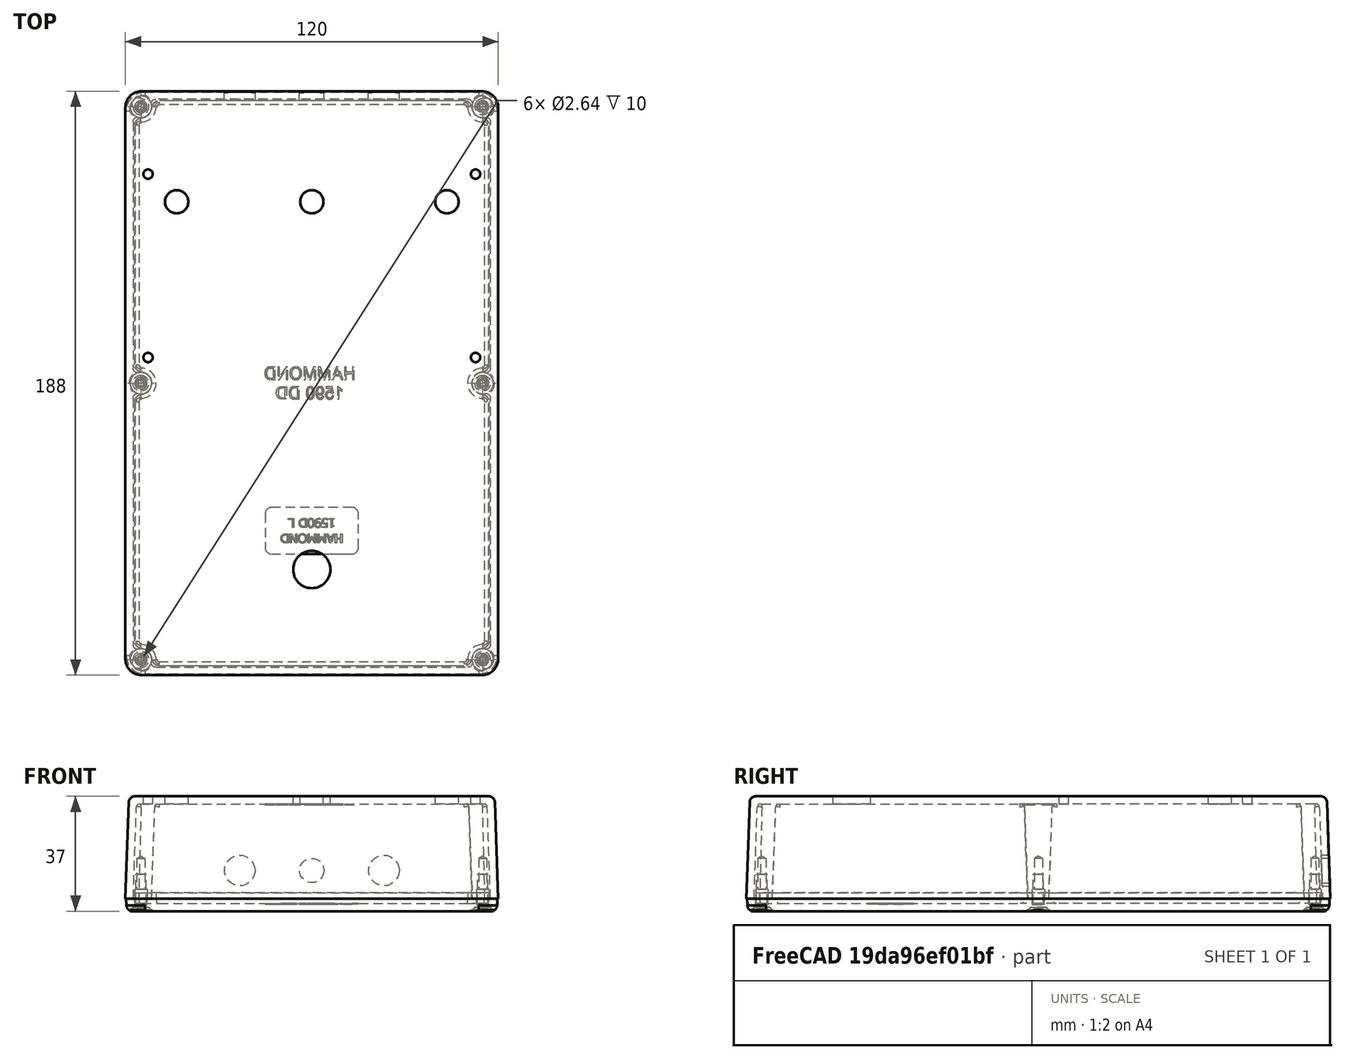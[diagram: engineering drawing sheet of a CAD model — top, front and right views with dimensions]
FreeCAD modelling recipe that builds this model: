
FCSTD DOCUMENT  (FreeCAD 0.19R18750 (Git))
Label: #000-000 - Mu-Tron Phasor II - STEP VRML Spreadsheet
License: All rights reserved
LicenseURL: http://en.wikipedia.org/wiki/All_rights_reserved
objects: Part::Cylinder×11, PartDesign::ShapeBinder×9, Part::Feature×8, App::Part×6, PartDesign::Plane×5, Part::MultiFuse×2, App::VRMLObject×2, PartDesign::Body×1, Part::Cut×1, Spreadsheet::Sheet×1
note: 37 computed .brp shape members not serialized (recipe doc carries the construction recipe); baked Part::Feature solids carry a one-line shape summary decoded from their .brp

FEATURE [PartDesign::Plane] DatumPlane  label="Origin_XY_DatumPlane"
  AttachmentOffset = pos=(-75,-100,0) rot=(0,0,1;0rad)
  Length = 122.361
  MapMode = 5
  Placement = pos=(-75,-100,0) rot=(0,0,1;0rad)
  ResizeMode = 1
  Support = -> [XY_Plane001]
  Width = 200
FEATURE [Part::Feature] Part__Feature  label="#700-001 - 1590DD Box"
  Placement = pos=(0,0,0) rot=(0.707107,0.707107,0;3.14159rad)
  shape: bbox 120 x 188 x 451.1 mm, 273 faces (baked)
FEATURE [Part::Feature] Part__Feature001  label="#700-001 - 1590DD - Lid"
  Placement = pos=(0,0,0) rot=(0,0.707107,0.707107;3.14159rad)
  shape: bbox 187.5 x 5.937 x 119.5 mm, 345 faces (baked)
FEATURE [Part::Feature] Part__Feature002  label="#700-001 - 1590DD - Screw 4/6"
  Placement = pos=(1.2e-14,1.5362,-55) rot=(0,1,0;0.650238rad)
  shape: bbox 6.871 x 11.85 x 6.871 mm, 25 faces (baked)
FEATURE [Part::Feature] Part__Feature003  label="#700-001 - 1590DD - Screw 2/6"
  Placement = pos=(-1.2e-14,1.5362,55) rot=(0,1,0;0.650238rad)
  shape: bbox 6.871 x 11.85 x 6.871 mm, 25 faces (baked)
FEATURE [Part::Feature] Part__Feature004  label="#700-001 - 1590DD - Screw 1/6"
  Placement = pos=(-89,1.5362,55) rot=(0,1,0;0.650238rad)
  shape: bbox 6.871 x 11.85 x 6.871 mm, 25 faces (baked)
FEATURE [Part::Feature] Part__Feature005  label="#700-001 - 1590DD - Screw 3/6"
  Placement = pos=(-89,1.5362,-55) rot=(0,-1,0;0.529817rad)
  shape: bbox 6.871 x 11.85 x 6.871 mm, 25 faces (baked)
FEATURE [Part::Feature] Part__Feature006  label="#700-001 - 1590DD - Screw 5/6"
  Placement = pos=(89,1.5362,55) rot=(0,0,1;0rad)
  shape: bbox 6.871 x 11.85 x 6.871 mm, 25 faces (baked)
FEATURE [Part::Feature] Part__Feature007  label="#700-001 - 1590DD - Screw 6/6"
  Placement = pos=(89,1.5362,-55) rot=(0,0,1;0rad)
  shape: bbox 6.871 x 11.85 x 6.871 mm, 25 faces (baked)
FEATURE [Part::MultiFuse] Fusion  label="#700-000 - Enclosure - Lid & Screws, Fusion"
  Placement = pos=(0,0,0) rot=(0.57735,-0.57735,0.57735;4.18879rad)
  Shapes = -> [Part__Feature001,Part__Feature004,Part__Feature003,Part__Feature005,Part__Feature002,Part__Feature006,Part__Feature007]
FEATURE [Part::Cylinder] Cylinder  label="Drill - Potentiometer - Rate [D=7.5, X=-43.5, Y=58.42]"
  Angle = 360
  AttacherType = Attacher::AttachEngine3D
  Height = 10
  Placement = pos=(-43.498,58.42,25) rot=(0,0,1;0rad)
  Radius = 3.75
FEATURE [Part::Cylinder] Cylinder001  label="Drill - Potentiometer - Depth [D7.5, X=0.0, Y = 58.42]]"
  Angle = 360
  AttacherType = Attacher::AttachEngine3D
  Height = 10
  Placement = pos=(0,58.42,25) rot=(0,0,1;0rad)
  Radius = 3.75
FEATURE [Part::Cylinder] Cylinder002  label="Drill - Potentiometer - Feedback [D=7.5, X=43.5, Y=58.42]"
  Angle = 360
  AttacherType = Attacher::AttachEngine3D
  Height = 10
  Placement = pos=(43.498,58.42,25) rot=(0,0,1;0rad)
  Radius = 3.75
FEATURE [PartDesign::Plane] DatumPlane001  label="Enclosure_Face_XY_DatumPlane"
  Length = 60
  MapMode = 5
  Placement = pos=(0,0,30.5) rot=(1,0,0;3.14159rad)
  ResizeMode = 0
  Width = 60
FEATURE [Part::Cylinder] Cylinder003  label="Drill - Standoff 4/4 [D=3.0, X=-52.705, Y=8.26]"
  Angle = 360
  AttacherType = Attacher::AttachEngine3D
  Height = 10
  Placement = pos=(-52.705,8.26,26) rot=(0,0,1;0rad)
  Radius = 1.5
FEATURE [Part::Cylinder] Cylinder004  label="Drill - Standoff 3/4 [D=3.0, X=52.705, Y=8.26]"
  Angle = 360
  AttacherType = Attacher::AttachEngine3D
  Height = 10
  Placement = pos=(52.705,8.26,26) rot=(0,0,1;0rad)
  Radius = 1.5
FEATURE [Part::Cylinder] Cylinder005  label="Drill - Standoff 2/4 [D=3.0, X=-52.705, Y=67.31]"
  Angle = 360
  AttacherType = Attacher::AttachEngine3D
  Height = 10
  Placement = pos=(-52.705,67.31,26) rot=(0,0,1;0rad)
  Radius = 1.5
FEATURE [Part::Cylinder] Cylinder006  label="Drill - Standoff 1/4 [D=3.0, X=52.705, Y=67.31]"
  Angle = 360
  AttacherType = Attacher::AttachEngine3D
  Height = 10
  Placement = pos=(52.705,67.31,26) rot=(0,0,1;0rad)
  Radius = 1.5
FEATURE [App::Part] Part001  label="#700-000 - Enclosure - Lid & Screws"
  Group = -> [Part__Feature004,Part__Feature007,Part__Feature005,Part__Feature001,Part__Feature003,Part__Feature006,Part__Feature002,Fusion]
  Origin = -> Origin002
  Placement = pos=(0,0,0) rot=(0,0,1;3.14159rad)
FEATURE [PartDesign::ShapeBinder] ShapeBinder  label="Enclosure_Lid_Inside"
  Placement = pos=(0,0,0) rot=(0.707107,0.707107,0;3.14159rad)
  Support = -> [Fusion]
  TraceSupport = false
FEATURE [PartDesign::ShapeBinder] ShapeBinder001  label="Enclosure_Lid_Lip"
  Placement = pos=(0,0,0) rot=(0.707107,0.707107,0;3.14159rad)
  Support = -> [Fusion]
  TraceSupport = false
FEATURE [PartDesign::ShapeBinder] ShapeBinder002  label="Enclosure_Lid_Outside"
  Placement = pos=(0,0,0) rot=(0.707107,0.707107,0;3.14159rad)
  Support = -> [Fusion]
  TraceSupport = false
FEATURE [PartDesign::ShapeBinder] ShapeBinder003  label="Enclosure_Box_Top_Outside"
  Placement = pos=(0,0,0) rot=(0.707107,0.707107,0;3.14159rad)
  Support = -> [Part__Feature]
  TraceSupport = false
FEATURE [PartDesign::ShapeBinder] ShapeBinder004  label="Enclosure_Box_Top_Inside"
  Placement = pos=(0,0,0) rot=(0.707107,0.707107,0;3.14159rad)
  Support = -> [Part__Feature]
  TraceSupport = false
FEATURE [PartDesign::ShapeBinder] ShapeBinder005  label="Enclosure_Box_Rear_Outside"
  Placement = pos=(0,0,0) rot=(0.707107,0.707107,0;3.14159rad)
  Support = -> [Part__Feature]
  TraceSupport = false
FEATURE [PartDesign::ShapeBinder] ShapeBinder006  label="Enclosure_Box_Rear_Inside"
  Placement = pos=(0,0,0) rot=(0.707107,0.707107,0;3.14159rad)
  Support = -> [Part__Feature]
  TraceSupport = false
FEATURE [PartDesign::ShapeBinder] ShapeBinder007  label="Enclosure_Box_Front_Outside"
  Placement = pos=(0,0,0) rot=(0.707107,0.707107,0;3.14159rad)
  Support = -> [Part__Feature]
  TraceSupport = false
FEATURE [PartDesign::ShapeBinder] ShapeBinder008  label="Enclosure_Box_Front_Inside"
  Placement = pos=(0,0,0) rot=(0.707107,0.707107,0;3.14159rad)
  Support = -> [Part__Feature]
  TraceSupport = false
FEATURE [Part::Cylinder] Cylinder007  label="Drill - Audio Jack 1/2 [D=10.0, X=-23.2, Z=9.1]"
  Angle = 360
  AttacherType = Attacher::AttachEngine3D
  Height = 10
  Placement = pos=(-23.2,90,9.1) rot=(-1,0,0;1.5708rad)
  Radius = 5
  expr: .Placement.Base.z = 1 + 1.6000000000000001 + 6.5
FEATURE [Part::Cylinder] Cylinder008  label="Drill - Audio Jack 2/2 [D=10.0, X=23.2, Z=9.1]"
  Angle = 360
  AttacherType = Attacher::AttachEngine3D
  Height = 10
  Placement = pos=(23.2,90,9.1) rot=(-1,0,0;1.5708rad)
  Radius = 5
  expr: .Placement.Base.z = 1 + 1.6000000000000001 + 6.5
FEATURE [Part::Cylinder] Cylinder009  label="Drill - Power Jack [D=8.0, X=0.0, Y=9.1]"
  Angle = 360
  AttacherType = Attacher::AttachEngine3D
  Height = 10
  Placement = pos=(0,90,9.1) rot=(-1,0,0;1.5708rad)
  Radius = 4
FEATURE [PartDesign::Plane] DatumPlane002  label="DatumPlane_Rear_Inside"
  Length = 60.17
  MapMode = 5
  Placement = pos=(2.03e-14,91.387,3.19131) rot=(0,0.71934,-0.694658;3.14159rad)
  ResizeMode = 0
  Support = -> [ShapeBinder006]
  Width = 61.8845
FEATURE [PartDesign::Plane] DatumPlane003  label="DatumPlane_Top_Inside"
  Length = 60
  MapMode = 5
  Placement = pos=(0,0,30.5) rot=(0.707107,0.707107,0;3.14159rad)
  ResizeMode = 0
  Support = -> [ShapeBinder004]
  Width = 60
FEATURE [PartDesign::Plane] DatumPlane004  label="DatumPlane_Lid_Inside"
  Length = 60
  MapMode = 5
  Placement = pos=(0,0,-1.5) rot=(0,0,1;1.5708rad)
  ResizeMode = 0
  Support = -> [ShapeBinder]
  Width = 60
FEATURE [PartDesign::Body] Body  label="Datum References"
  Group = -> [DatumPlane,DatumPlane001,ShapeBinder,ShapeBinder001,ShapeBinder002,ShapeBinder003,ShapeBinder004,ShapeBinder005,ShapeBinder006,ShapeBinder007,ShapeBinder008,DatumPlane002,DatumPlane003,DatumPlane004]
  Origin = -> Origin001
FEATURE [App::Part] Part003  label="#700-000 - Datum References"
  Group = -> [Body]
  Origin = -> Origin004
FEATURE [Part::Cylinder] Cylinder010  label="Drill - Footswitch [D=12.0, X=0.0, Y=-60.0]"
  Angle = 360
  AttacherType = Attacher::AttachEngine3D
  Height = 10
  Placement = pos=(0,-60,25) rot=(0,0,1;0rad)
  Radius = 6
FEATURE [Part::MultiFuse] Fusion001  label="Drills"
  Shapes = -> [Cylinder,Cylinder002,Cylinder001,Cylinder003,Cylinder004,Cylinder005,Cylinder006,Cylinder007,Cylinder008,Cylinder009,Cylinder010]
FEATURE [Part::Cut] Cut  label="#700-000 - Enclosure - Box, Drilled"
  Base = -> Part__Feature
  Tool = -> Fusion001
FEATURE [App::Part] Part002  label="#700-000 - Enclosure - Box, Machined"
  Group = -> [Part__Feature,Fusion001,Cylinder002,Cylinder006,Cylinder004,Cylinder005,Cylinder,Cylinder001,Cylinder003,Cut]
  Origin = -> Origin003
FEATURE [App::Part] Part  label="#700-000-A - Enclosure [1590DD, Portrait] - STEP"
  Group = -> [Part001,Part002,Part003]
  Origin = -> Origin
FEATURE [App::VRMLObject] _700_000_A___Enclosure___Box__1590DD__Portrait_  label="#700-000-A - Enclosure - Box [1590DD, Portrait]"
FEATURE [App::VRMLObject] _700_000_A___Enclosure___Lid__1590DD__Portrait_  label="#700-000-A - Enclosure - Lid [1590DD, Portrait]"
FEATURE [App::Part] Part004  label="#700-000-A - Enclosure [1590DD, Portrait] - VRML"
  Group = -> [_700_000_A___Enclosure___Box__1590DD__Portrait_,_700_000_A___Enclosure___Lid__1590DD__Portrait_]
  Origin = -> Origin005
FEATURE [App::Part] Part005  label="#000-000 - Final Assembly"
  Origin = -> Origin006
FEATURE [Spreadsheet::Sheet] Spreadsheet
